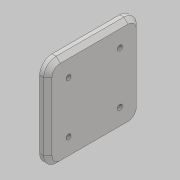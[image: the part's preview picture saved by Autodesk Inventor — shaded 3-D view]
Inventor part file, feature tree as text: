
AUTODESK INVENTOR PART (.ipt)
format: ipt  version: 2018 (Build 220112000, 112)  size: 124,416 bytes
history: native  units: mm
features: sketch x3, hole x2, other x1, extrude x1, fillet x1, chamfer x1, projected_geometry x1
ambient origin geometry x8: Origin, YZ Plane, XZ Plane, XY Plane, X Axis, Y Axis, Z Axis, Center Point
bodies: Body1 (feature_tree)
feature tree (10):
  other  "實體1"
  extrude  "擠出1"  Depth=225.0mm
  fillet  "圓角1"  Radius=225.0mm
  chamfer  "倒角1"  Distance=20.0mm
  hole  "孔1"  [1 undecoded]
  hole  "孔2"  [1 undecoded]
  sketch  "草圖1"
  sketch  "草圖2"
  sketch  "草圖3"
  projected_geometry  "投影迴路1"
note: 2 required parameter values undecoded (feature->parameter linkage not recoverable at this tier; creation-order binding heuristic only, values carry confidence <= 0.55)
